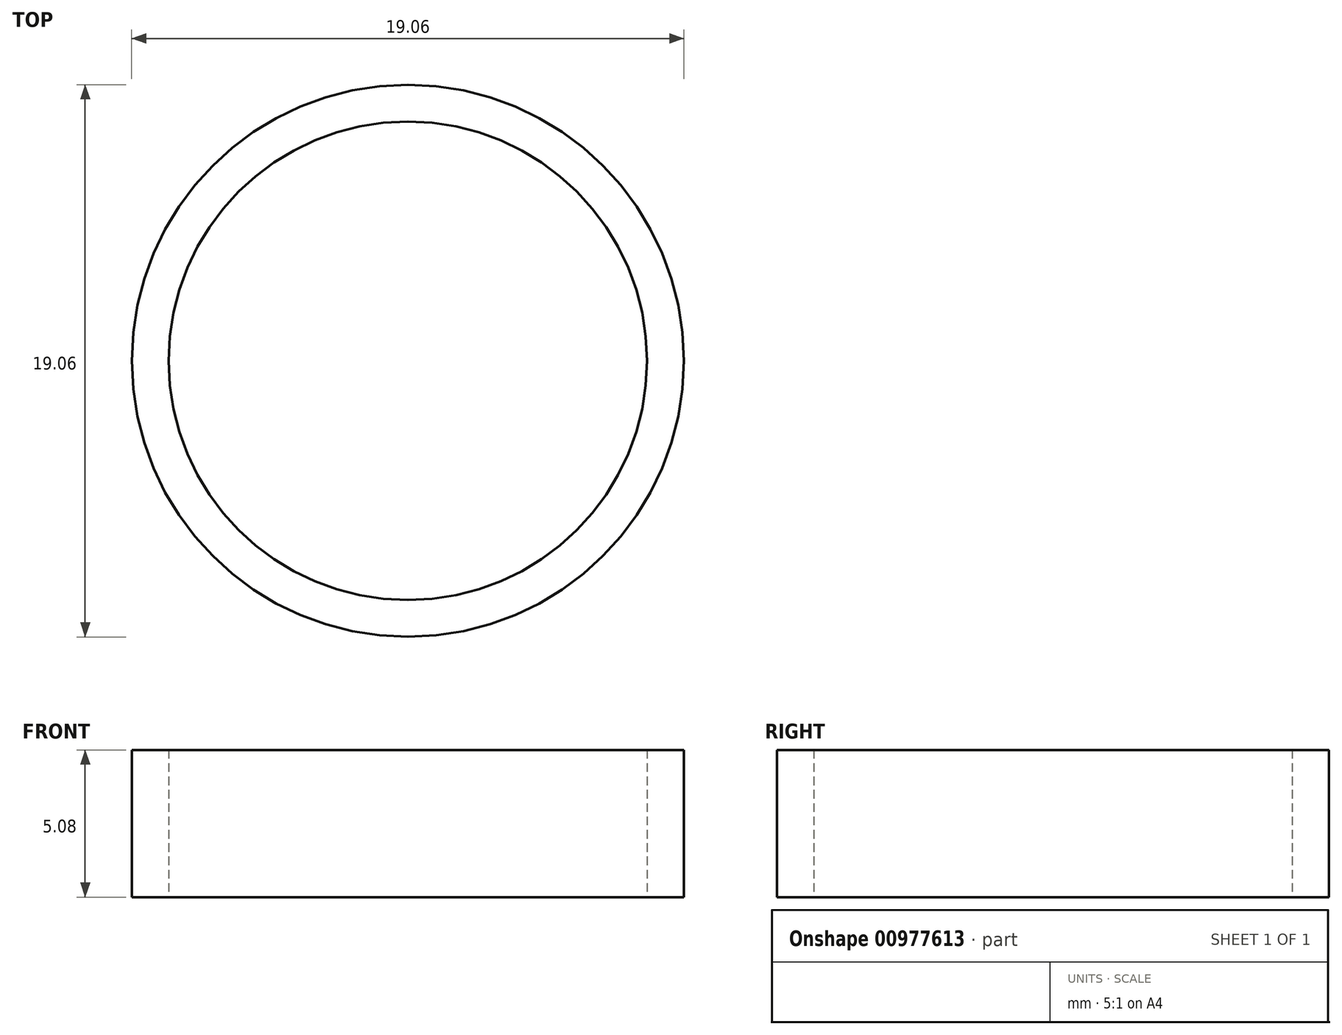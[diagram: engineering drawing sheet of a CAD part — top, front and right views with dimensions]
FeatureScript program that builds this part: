
annotation { "Feature Type Name" : "Feature", "Feature Type Description" : "" }
export const myFeature = defineFeature(function(context is Context, id is Id, definition is map)
    precondition{}
    {
        {
            var Q0;
            Q0=qCreatedBy(makeId("Top.planeOp"),FACE);
            var sketch = newSketch(context, id + "F0", { "sketchPlane" : qUnion([Q0])});
            skCircle(sketch, "E0", {"center": v(0, 0) * mm, "radius": 9.53 * mm});
            skCircle(sketch, "E1", {"center": v(0, 0) * mm, "radius": 8.26 * mm});
            skSolve(sketch);
        }
        {
            var Q0;
            Q0=makeQuery(id+"F0.imprint","IMPRINT",FACE,{"disambiguationData":[TD([[makeQuery(id+"F0.imprint","IMPRINT",EDGE,{"derivedFrom":sQuery(id+"F0.wireOp",EDGE,"E0")}),1.0]])]});
            extrude(context, id + "F1", {"entities" : qUnion([Q0]), "depth" : 5.08 * mm, "offsetDistance" : 25.4 * mm});
        }
    });
